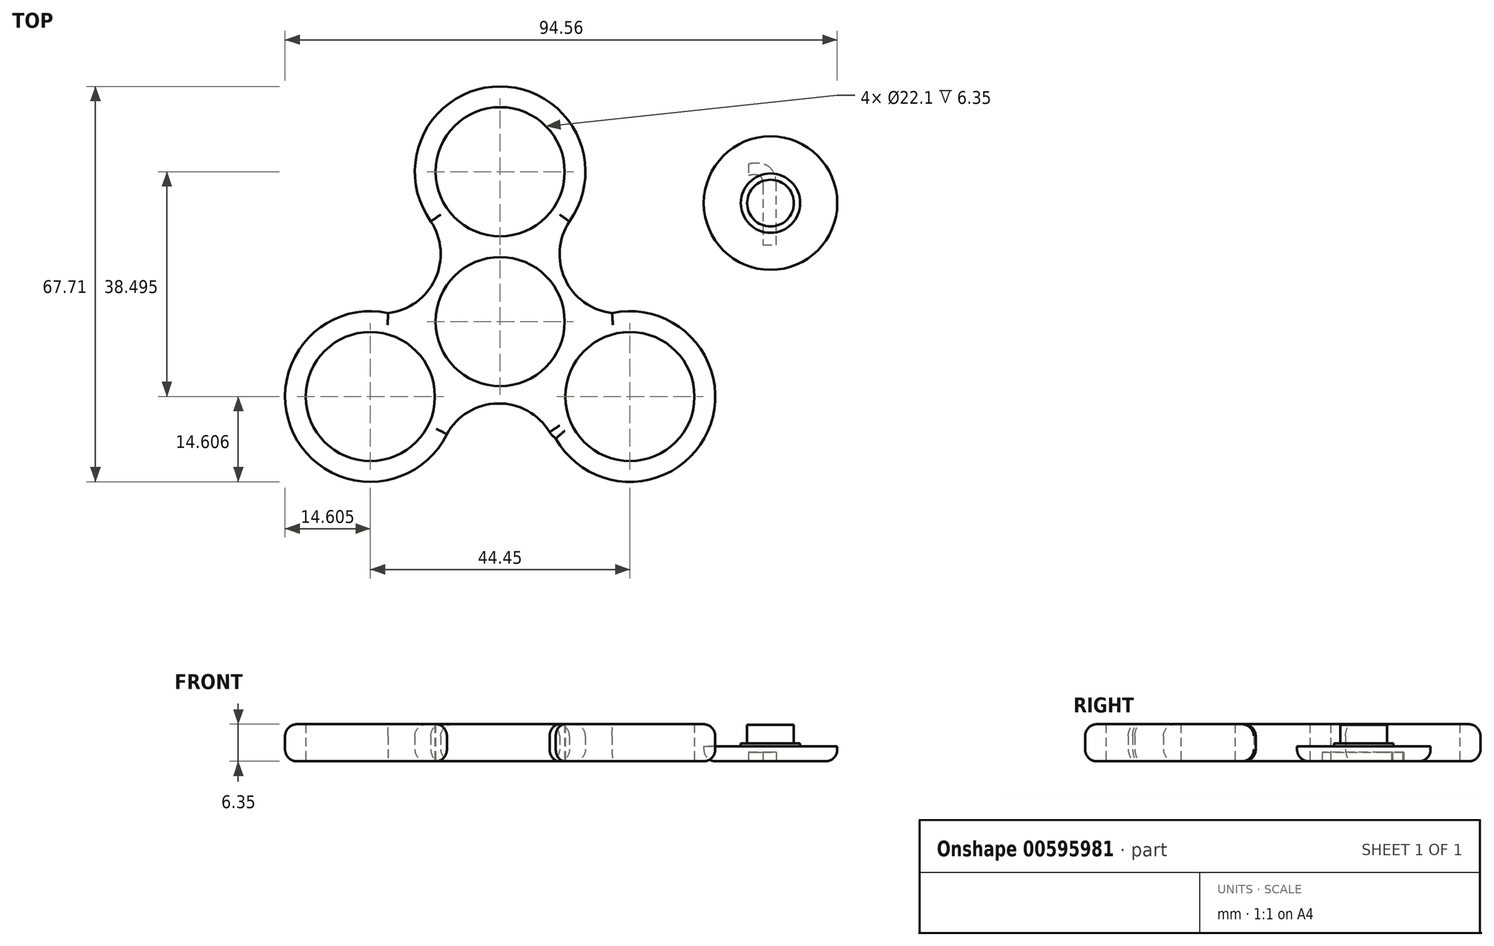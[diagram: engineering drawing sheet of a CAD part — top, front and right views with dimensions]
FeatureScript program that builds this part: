
annotation { "Feature Type Name" : "Feature", "Feature Type Description" : "" }
export const myFeature = defineFeature(function(context is Context, id is Id, definition is map)
    precondition{}
    {
        {
            var Q0;
            Q0=qCreatedBy(makeId("Top.planeOp"),FACE);
            var sketch = newSketch(context, id + "F0", { "sketchPlane" : qUnion([Q0])});
            skCircle(sketch, "E0", {"center": v(0, 60.07) * mm, "radius": 11.05 * mm});
            skCircle(sketch, "E1.1.0", {"center": v(-22.23, 21.58) * mm, "radius": 11.05 * mm});
            skCircle(sketch, "E1.2.0", {"center": v(22.22, 21.58) * mm, "radius": 11.05 * mm});
            skPoint(sketch, "E1.center", {"position": v(0, 34.4) * mm});
            skCircle(sketch, "E2", {"center": v(0, 34.4) * mm, "radius": 11.05 * mm});
            skArc(sketch, "E3", {"start": v(11.87, 51.56) * mm, "mid": v(0, 74.68) * mm, "end": v(-11.87, 51.56) * mm});
            skArc(sketch, "E4", {"start": v(-19.17, 35.86) * mm, "mid": v(-35.37, 15.2) * mm, "end": v(-9.12, 15.12) * mm});
            skArc(sketch, "E5", {"start": v(9.52, 14.37) * mm, "mid": v(35.55, 15.6) * mm, "end": v(19.17, 35.86) * mm});
            skArc(sketch, "E6", {"start": v(-19.17, 35.86) * mm, "mid": v(-11.13, 41.67) * mm, "end": v(-11.87, 51.56) * mm});
            skArc(sketch, "E7.MirrorCS", {"start": v(19.17, 35.86) * mm, "mid": v(11.13, 41.67) * mm, "end": v(11.87, 51.56) * mm});
            skArc(sketch, "E8", {"start": v(8.47, 15.5) * mm, "mid": v(-0.7, 20.38) * mm, "end": v(-9.37, 14.64) * mm});
            skArc(sketch, "E9", {"start": v(8.47, 15.5) * mm, "mid": v(8.95, 14.9) * mm, "end": v(9.52, 14.37) * mm});
            skSolve(sketch);
        }
        {
            var Q0;
            Q0 = qSketchRegion(id + "F0", true);
            extrude(context, id + "F1", {"entities" : qUnion([Q0]), "depth" : 6.35 * mm, "offsetDistance" : 25.4 * mm});
        }
        {
            var Q0;
            Q0=makeQuery(id+"F1.opExtrude","CAP_EDGE",EDGE,{"disambiguationData":[OSD([sQuery(id+"F0.wireOp",EDGE,"E4")])],"isStart":false});
            var Q1;
            Q1=makeQuery(id+"F1.opExtrude","CAP_EDGE",EDGE,{"disambiguationData":[OSD([sQuery(id+"F0.wireOp",EDGE,"E8")])],"isStart":false});
            var Q2;
            Q2=makeQuery(id+"F1.opExtrude","CAP_EDGE",EDGE,{"disambiguationData":[OSD([sQuery(id+"F0.wireOp",EDGE,"E7.MirrorCS")])],"isStart":false});
            var Q3;
            Q3=makeQuery(id+"F1.opExtrude","CAP_EDGE",EDGE,{"disambiguationData":[OSD([sQuery(id+"F0.wireOp",EDGE,"E3")])],"isStart":false});
            var Q4;
            Q4=makeQuery(id+"F1.opExtrude","CAP_EDGE",EDGE,{"disambiguationData":[OSD([sQuery(id+"F0.wireOp",EDGE,"E6")])],"isStart":false});
            var Q5;
            Q5=makeQuery(id+"F1.opExtrude","CAP_EDGE",EDGE,{"disambiguationData":[OSD([sQuery(id+"F0.wireOp",EDGE,"E5")])],"isStart":false});
            var Q6;
            Q6=makeQuery(id+"F1.opExtrude","CAP_EDGE",EDGE,{"disambiguationData":[OSD([sQuery(id+"F0.wireOp",EDGE,"E9")])],"isStart":false});
            var Q7;
            Q7=makeQuery(id+"F1.opExtrude","CAP_EDGE",EDGE,{"disambiguationData":[OSD([sQuery(id+"F0.wireOp",EDGE,"E4")])],"isStart":true});
            var Q8;
            Q8=makeQuery(id+"F1.opExtrude","CAP_EDGE",EDGE,{"disambiguationData":[OSD([sQuery(id+"F0.wireOp",EDGE,"E6")])],"isStart":true});
            var Q9;
            Q9=makeQuery(id+"F1.opExtrude","CAP_EDGE",EDGE,{"disambiguationData":[OSD([sQuery(id+"F0.wireOp",EDGE,"E3")])],"isStart":true});
            var Q10;
            Q10=makeQuery(id+"F1.opExtrude","CAP_EDGE",EDGE,{"disambiguationData":[OSD([sQuery(id+"F0.wireOp",EDGE,"E7.MirrorCS")])],"isStart":true});
            var Q11;
            Q11=makeQuery(id+"F1.opExtrude","CAP_EDGE",EDGE,{"disambiguationData":[OSD([sQuery(id+"F0.wireOp",EDGE,"E5")])],"isStart":true});
            var Q12;
            Q12=makeQuery(id+"F1.opExtrude","CAP_EDGE",EDGE,{"disambiguationData":[OSD([sQuery(id+"F0.wireOp",EDGE,"E9")])],"isStart":true});
            fillet(context, id + "F2", {"entities" : qUnion([Q0, Q1, Q2, Q3, Q4, Q5, Q6, Q7, Q8, Q9, Q10, Q11, Q12]), "radius" : 2.03 * mm, "tangentPropagation" : true, "allowEdgeOverflow" : false});
        }
        {
            var Q0;
            Q0=qCreatedBy(makeId("Top.planeOp"),FACE);
            var sketch = newSketch(context, id + "F3", { "sketchPlane" : qUnion([Q0])});
            skCircle(sketch, "E10", {"center": v(46.3, 54.7) * mm, "radius": 11.43 * mm});
            skSolve(sketch);
        }
        {
            var Q0;
            Q0=makeQuery(id+"F3.imprint","IMPRINT",FACE,{"disambiguationData":[TD([[makeQuery(id+"F3.imprint","IMPRINT",EDGE,{"derivedFrom":sQuery(id+"F3.wireOp",EDGE,"E10")}),1.0]])]});
            extrude(context, id + "F4", {"entities" : qUnion([Q0]), "depth" : 2.54 * mm, "offsetDistance" : 25.4 * mm});
        }
        {
            var Q0;
            Q0=makeQuery(id+"F4.opExtrude","CAP_FACE",FACE,{"disambiguationData":[OSD([sQuery(id+"F3.wireOp",EDGE,"E10")])],"isStart":false});
            var sketch = newSketch(context, id + "F5", { "sketchPlane" : qUnion([Q0])});
            skCircle(sketch, "E11", {"center": v(46.3, 54.7) * mm, "radius": 5.08 * mm});
            skSolve(sketch);
        }
        {
            var Q0;
            Q0=makeQuery(id+"F5.imprint","IMPRINT",FACE,{"disambiguationData":[TD([[makeQuery(id+"F5.imprint","IMPRINT",EDGE,{"derivedFrom":sQuery(id+"F5.wireOp",EDGE,"E11")}),1.0]])]});
            extrude(context, id + "F6", {"entities" : qUnion([Q0]), "operationType" : NewBodyOperationType.ADD, "depth" : 0.5 * mm, "offsetDistance" : 25.4 * mm});
        }
        {
            var Q0;
            Q0=makeQuery(id+"F4.opExtrude","CAP_EDGE",EDGE,{"disambiguationData":[OSD([sQuery(id+"F3.wireOp",EDGE,"E10")])],"isStart":true});
            fillet(context, id + "F7", {"entities" : qUnion([Q0]), "radius" : 2.03 * mm, "tangentPropagation" : true, "allowEdgeOverflow" : false});
        }
        {
            var Q0;
            Q0=makeQuery(id+"F4.opExtrude","CAP_FACE",FACE,{"disambiguationData":[OSD([sQuery(id+"F3.wireOp",EDGE,"E10")])],"isStart":true});
            var sketch = newSketch(context, id + "F8", { "sketchPlane" : qUnion([Q0])});
            skText(sketch, "E12", { "text": "J", "fontName": "OpenSans-Bold.ttf"});
            const initialGuessF8  = {"E12": [0.04364, -0.05835, 1, 0, 0.0109]};
            skSetInitialGuess(sketch, initialGuessF8);
            skSolve(sketch);
        }
        {
            var Q0;
            Q0 = qSketchRegion(id + "F8", true);
            extrude(context, id + "F9", {"entities" : qUnion([Q0]), "operationType" : NewBodyOperationType.REMOVE, "oppositeDirection" : true, "depth" : 1.52 * mm, "offsetDistance" : 25.4 * mm});
        }
        {
            var Q0;
            Q0=makeQuery(id+"F6.opExtrude","CAP_FACE",FACE,{"disambiguationData":[OSD([sQuery(id+"F5.wireOp",EDGE,"E11")])],"isStart":false});
            var sketch = newSketch(context, id + "F10", { "sketchPlane" : qUnion([Q0])});
            skCircle(sketch, "E13", {"center": v(46.3, 54.7) * mm, "radius": 4 * mm});
            skSolve(sketch);
        }
        {
            var Q0;
            Q0 = qSketchRegion(id + "F10", true);
            extrude(context, id + "F11", {"entities" : qUnion([Q0]), "operationType" : NewBodyOperationType.ADD, "depth" : 3.17 * mm, "offsetDistance" : 25.4 * mm});
        }
    });
